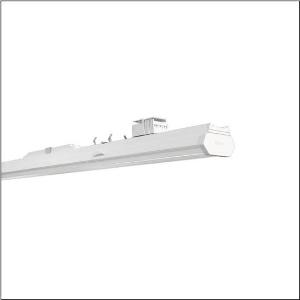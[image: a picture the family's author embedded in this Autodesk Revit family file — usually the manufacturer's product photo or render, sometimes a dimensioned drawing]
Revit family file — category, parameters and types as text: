
# Revit family: licross_r__21_protected_ho_52tp11dn4e5s_2e66
name_source: partatom
category: Lighting Fixtures
units: mm (PartAtom-declared; Revit-internal decimal feet)

## family parameters
Cut with Voids When Loaded = No
Host = Face
Light Source = No
Part Type = Normal
Room Calculation Point = No
Round Connector Dimension = Use Diameter
Shared = No

## types (1)
- --- (1 x LED, 14920 lm, 84.9 W, 4000K)
    Apparent Load = 85 VA
    CIE Flux Codes = 84 94 98 99 100
    Color Rendering = 80
    Color Temperature = 4000K
    Default Elevation = 1800 mm
    Description = Licross® 21 Protected HO, luminaire insert, of sheet steel, galvanised, coil coated, white, length: 1.500mm, width: 90mm, height: 103mm, LED rated luminous flux: 14.920lm, light colour: 840, SDCM (Standard Deviation of Colour Matching)MacAdam ≤ 3 SDCM (initial), control gear: DALI 2, with plug, 5-pole, with phase selection, mains connection: 220..240V, AC, 50/60Hz, rated input power: 85W, internal wiring halogen-free, primary light control with lens, of plastic, primary optical cover: cover, of PMMA, light emission: direct distribution, primary light characteristic: symmetric, protection rating (complete): IP64, insulation class (complete): insulation class I (protective earthing), certification: CE, ENEC, VDE, UKCA, protection symbol: D if used in an environment with conductive dust loads with corresponding accessories, impact resistance: IK06, permissible ambient temperature for indoor applications: -25..+35°C, corresponds to IFS (International Featured Standards) requirements for safety and quality in the food industry, reducing of maximum allowable ambient temperature of 5°C with ceiling mounting, LABS conformity tested according to VDMA 24364:2018-05, packaging unit: 1 piece
    Height = 92 mm
    Lamp = 1 x LED
    Lamp Light Flux = 14920 lm
    Lamp Power = 84.9 W
    Lamp count = 1
    Length = 1500 mm
    Luminous efficacy = 176 lm/W
    Manufacturer = Siteco
    ModVariant = No
    Model = 52TP11DN4E5S
    Mounting Place = Ceiling
    Mounting Type = Pendant
    Number of Poles = 1
    OnlyDefault = Yes
    Power Factor = 1
    Product Name = Licross® 21 Protected HO
    Product group = luminaire insert | ceiling pendant
    ProductGroupID = 901
    Protection Class = Protection class I
    Protection Degree = IP 64
    RLX_Detail_Level = 1
    RLX_Emergency_Light_Flux = 0 lm
    RLX_Emergency_Type = 0
    RLX_Emergency_Type_DB = No
    RlxData = <blob elided: 24545 chars, md5=4235b3f0>
    Socket = socket
    Standby Power = 0 W
    System Light Flux = 14920 lm
    System Power = 85 W
    Type Comments = factory setting: luminous flux: 100 % | dim-lin: 254 | 484 mA
    Type Image = l_1256148.jpg
    URL = http://relux.com
    VarID = @adj_132373
    Voltage = 0 V
    Weight = 0.00 kg
    Width = 88 mm

## geometry (parser evidence)
native form markers: Blend x4, Sweep x11
no freeform markers — native parametric forms only
